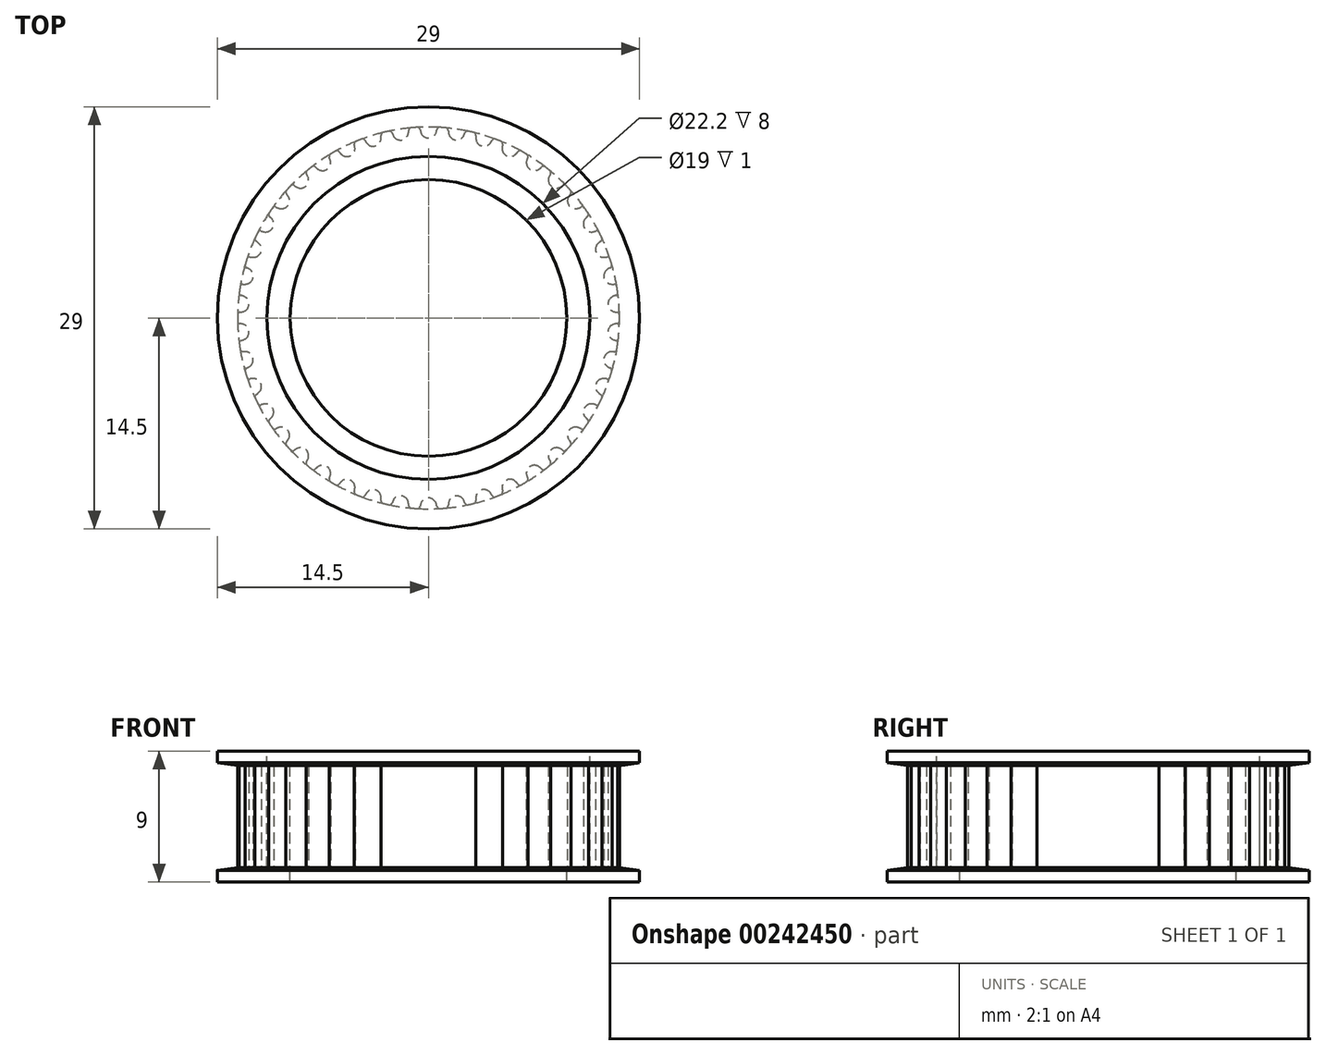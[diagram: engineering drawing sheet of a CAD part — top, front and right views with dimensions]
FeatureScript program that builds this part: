
annotation { "Feature Type Name" : "Feature", "Feature Type Description" : "" }
export const myFeature = defineFeature(function(context is Context, id is Id, definition is map)
    precondition{}
    {
        {
            assignVariable(context, id + "F0", {"name" : "teeth", "anyValue" : 42});
        }
        {
            assignVariable(context, id + "F1", {"name" : "belt_width", "anyValue" : 7});
        }
        {
            var Q0;
            Q0=qCreatedBy(makeId("Top.planeOp"),FACE);
            var sketch = newSketch(context, id + "F2", { "sketchPlane" : qUnion([Q0])});
            skLineSegment(sketch, "E0", {"start": v(0, 0) * mm, "end": v(0, 12.37) * mm, "construction": true});
            skCircle(sketch, "E1", {"center": v(0, 0) * mm, "radius": 13.12 * mm});
            skPoint(sketch, "E2.MirrorCS.end.orphan", {"position": v(0.98, 13.08) * mm});
            skLineSegment(sketch, "E3", {"start": v(0.98, 13.08) * mm, "end": v(1, 13.33) * mm, "construction": true});
            skLineSegment(sketch, "E4", {"start": v(-0.98, 13.08) * mm, "end": v(-1, 13.33) * mm, "construction": true});
            skArc(sketch, "E5", {"start": v(0, 12.37) * mm, "mid": v(0.34, 12.48) * mm, "end": v(0.54, 12.77) * mm});
            skArc(sketch, "E6", {"start": v(0.54, 12.77) * mm, "mid": v(0.56, 12.87) * mm, "end": v(0.58, 12.97) * mm, "construction": true});
            skLineSegment(sketch, "E7", {"start": v(0, 12.37) * mm, "end": v(0, 13.12) * mm, "construction": true});
            skLineSegment(sketch, "E8", {"start": v(0, 13.12) * mm, "end": v(0, 13.37) * mm, "construction": true});
            skArc(sketch, "E9", {"start": v(0.58, 12.97) * mm, "mid": v(0.64, 13.06) * mm, "end": v(0.74, 13.1) * mm, "construction": true});
            skArc(sketch, "E10", {"start": v(1, 13.33) * mm, "mid": v(0, 13.37) * mm, "end": v(-1, 13.33) * mm, "construction": true});
            skLineSegment(sketch, "E11", {"start": v(0.98, 13.08) * mm, "end": v(0.92, 12.33) * mm});
            skLineSegment(sketch, "E12", {"start": v(0.92, 12.33) * mm, "end": v(0, 0) * mm});
            skLineSegment(sketch, "E13", {"start": v(0, 0) * mm, "end": v(-0.92, 12.33) * mm});
            skLineSegment(sketch, "E14", {"start": v(-0.92, 12.33) * mm, "end": v(-0.98, 13.08) * mm});
            skArc(sketch, "E15", {"start": v(0.77, 13.1) * mm, "mid": v(0.65, 13.06) * mm, "end": v(0.58, 12.95) * mm});
            skArc(sketch, "E16", {"start": v(0.54, 12.77) * mm, "mid": v(0.56, 12.86) * mm, "end": v(0.58, 12.95) * mm});
            skArc(sketch, "E17.MirrorCS", {"start": v(0, 12.37) * mm, "mid": v(-0.34, 12.48) * mm, "end": v(-0.54, 12.77) * mm});
            skArc(sketch, "E18.MirrorCS", {"start": v(-0.54, 12.77) * mm, "mid": v(-0.56, 12.86) * mm, "end": v(-0.58, 12.95) * mm});
            skArc(sketch, "E19.MirrorCS", {"start": v(-0.77, 13.1) * mm, "mid": v(-0.65, 13.06) * mm, "end": v(-0.58, 12.95) * mm});
            skArc(sketch, "E20", {"start": v(0, 13.12) * mm, "mid": v(-0.2, 13.11) * mm, "end": v(-0.4, 13.1) * mm});
            skArc(sketch, "E21", {"start": v(0.92, 12.33) * mm, "mid": v(0, 12.37) * mm, "end": v(-0.92, 12.33) * mm, "construction": true});
            skLineSegment(sketch, "E22", {"start": v(1, 13.33) * mm, "end": v(1.03, 13.7) * mm, "construction": true});
            skLineSegment(sketch, "E23", {"start": v(-1, 13.33) * mm, "end": v(-1.03, 13.7) * mm, "construction": true});
            skArc(sketch, "E24", {"start": v(-1.03, 13.7) * mm, "mid": v(0, 13.75) * mm, "end": v(1.03, 13.7) * mm, "construction": true});
            skSolve(sketch);
        }
        {
            var Q0;
            Q0=makeQuery(id+"F2.imprint","IMPRINT",FACE,{"disambiguationData":[TD([[makeQuery(id+"F2.imprint","IMPRINT",EDGE,{"derivedFrom":sQuery(id+"F2.wireOp",EDGE,"E5")}),-1.0]])]});
            var Q1;
            {var subQ1=sQuery(id+"F2.wireOp",EDGE,"E14");Q1=makeQuery(id+"F2.imprint","IMPRINT",FACE,{"disambiguationData":[TD([[makeQuery(id+"F2.imprint","IMPRINT",EDGE,{"derivedFrom":subQ1}),-1.0]])]});}
            var Q2;
            {var subQ0=sQuery(id+"F2.wireOp",EDGE,"E12");Q2=makeQuery(id+"F2.imprint","IMPRINT",FACE,{"disambiguationData":[TD([[makeQuery(id+"F2.imprint","IMPRINT",EDGE,{"derivedFrom":subQ0}),-1.0]])]});}
            extrude(context, id + "F3", {"entities" : qUnion([Q0, Q1, Q2]), "depth" : (getVariable(context, 'belt_width')) * mm, "symmetric" : true});
        }
        {
            var Q0;
            Q0=makeQuery(id+"F3.opExtrude","SWEPT_BODY",BODY,{"disambiguationData":[OSD([sQuery(id+"F2.wireOp",EDGE,"E1"),sQuery(id+"F2.wireOp",EDGE,"E5"),sQuery(id+"F2.wireOp",EDGE,"E11"),sQuery(id+"F2.wireOp",EDGE,"E12"),sQuery(id+"F2.wireOp",EDGE,"E13"),sQuery(id+"F2.wireOp",EDGE,"E14"),sQuery(id+"F2.wireOp",EDGE,"E15"),sQuery(id+"F2.wireOp",EDGE,"E16"),sQuery(id+"F2.wireOp",EDGE,"E17.MirrorCS"),sQuery(id+"F2.wireOp",EDGE,"E18.MirrorCS"),sQuery(id+"F2.wireOp",EDGE,"E19.MirrorCS")])]});
            var Q1;
            Q1=makeQuery(id+"F3.opExtrude","SWEPT_EDGE",EDGE,{"disambiguationData":[OSD([sQuery(id+"F2.wireOp",EDGE,"E12"),sQuery(id+"F2.wireOp",EDGE,"E13")])]});
            circularPattern(context, id + "F4", {"operationType" : NewBodyOperationType.ADD, "entities" : qUnion([Q0]), "axis" : qUnion([Q1]), "angle" : 360 * degree, "instanceCount" : getVariable(context, 'teeth'), "equalSpace" : true, "computeTransformsWithoutBuiltin" : true});
        }
        {
            var Q0;
            Q0=qCreatedBy(makeId("Front.planeOp"),FACE);
            var sketch = newSketch(context, id + "F5", { "sketchPlane" : qUnion([Q0])});
            skLineSegment(sketch, "E25", {"start": v(0, -3.5) * mm, "end": v(13.12, -3.5) * mm});
            skLineSegment(sketch, "E26", {"start": v(13.12, -3.5) * mm, "end": v(14.5, -3.7) * mm});
            skLineSegment(sketch, "E27", {"start": v(0, 3.5) * mm, "end": v(13.12, 3.5) * mm});
            skLineSegment(sketch, "E28", {"start": v(14.5, 3.7) * mm, "end": v(13.12, 3.5) * mm});
            skLineSegment(sketch, "E29", {"start": v(14.5, 3.7) * mm, "end": v(14.5, 4.5) * mm});
            skLineSegment(sketch, "E30", {"start": v(14.5, 4.5) * mm, "end": v(0, 4.5) * mm});
            skLineSegment(sketch, "E31", {"start": v(0, 4.5) * mm, "end": v(0, 3.5) * mm});
            skLineSegment(sketch, "E32", {"start": v(13.12, -3.5) * mm, "end": v(14.5, -3.5) * mm, "construction": true});
            skLineSegment(sketch, "E33", {"start": v(14.5, -3.5) * mm, "end": v(14.5, -3.7) * mm, "construction": true});
            skLineSegment(sketch, "E34", {"start": v(13.12, 3.5) * mm, "end": v(14.5, 3.5) * mm, "construction": true});
            skLineSegment(sketch, "E35", {"start": v(14.5, 3.5) * mm, "end": v(14.5, 3.7) * mm, "construction": true});
            skLineSegment(sketch, "E36", {"start": v(13.12, 0) * mm, "end": v(13.12, -3.5) * mm, "construction": true});
            skLineSegment(sketch, "E37", {"start": v(14.5, -4.5) * mm, "end": v(0, -4.5) * mm});
            skLineSegment(sketch, "E38", {"start": v(14.5, -3.7) * mm, "end": v(14.5, -4.5) * mm});
            skLineSegment(sketch, "E39", {"start": v(0, -3.5) * mm, "end": v(0, -4.5) * mm});
            skLineSegment(sketch, "E40", {"start": v(0, 4.5) * mm, "end": v(0, -4.5) * mm, "construction": true});
            skSolve(sketch);
        }
        {
            var Q0;
            Q0=makeQuery(id+"F5.imprint","IMPRINT",FACE,{"disambiguationData":[TD([[makeQuery(id+"F5.imprint","IMPRINT",EDGE,{"derivedFrom":sQuery(id+"F5.wireOp",EDGE,"E25")}),-1.0]])]});
            var Q1;
            Q1=makeQuery(id+"F5.imprint","IMPRINT",FACE,{"disambiguationData":[TD([[makeQuery(id+"F5.imprint","IMPRINT",EDGE,{"derivedFrom":sQuery(id+"F5.wireOp",EDGE,"E27")}),1.0]])]});
            var Q2;
            Q2=qConstructionFilter(qBodyType(qCreatedBy(id+"F5",EDGE),BodyType.WIRE),ConstructionObject.NO);
            var Q3;
            Q3=sQuery(id+"F5.wireOp",EDGE,"E40");
            revolve(context, id + "F6", {"operationType" : NewBodyOperationType.ADD, "entities" : qUnion([Q0, Q1]), "surfaceEntities" : qUnion([Q2]), "axis" : qUnion([Q3]), "revolveType" : RevolveType.FULL});
        }
        {
            var Q0;
            Q0=makeQuery(id+"F6.opRevolve","SWEPT_FACE",FACE,{"disambiguationData":[OSD([sQuery(id+"F5.wireOp",EDGE,"E30")])]});
            var sketch = newSketch(context, id + "F7", { "sketchPlane" : qUnion([Q0])});
            skPoint(sketch, "E41", {"position": v(0, 0) * mm});
            skCircle(sketch, "E42", {"center": v(0, 0) * mm, "radius": 11.1 * mm});
            skCircle(sketch, "E43", {"center": v(0, 0) * mm, "radius": 9.5 * mm});
            skSolve(sketch);
        }
        {
            var Q0;
            Q0=makeQuery(id+"F7.imprint","IMPRINT",FACE,{"disambiguationData":[TD([[makeQuery(id+"F7.imprint","IMPRINT",EDGE,{"derivedFrom":sQuery(id+"F7.wireOp",EDGE,"E42")}),1.0]])]});
            extrude(context, id + "F8", {"entities" : qUnion([Q0]), "operationType" : NewBodyOperationType.REMOVE, "oppositeDirection" : true, "depth" : 8 * mm});
        }
        {
            var Q0;
            Q0=makeQuery(id+"F8.boolean.opBoolean","SPLIT",FACE,{"disambiguationData":[TD([makeQuery(id+"F8.opExtrude","SWEPT_FACE",FACE,{"disambiguationData":[OSD([sQuery(id+"F7.wireOp",EDGE,"E43")])]})])],"derivedFrom":makeQuery(id+"F6.opRevolve","SWEPT_FACE",FACE,{"disambiguationData":[OSD([sQuery(id+"F5.wireOp",EDGE,"E30")])]})});
            extrude(context, id + "F9", {"entities" : qUnion([Q0]), "operationType" : NewBodyOperationType.REMOVE, "endBound" : BoundingType.UP_TO_NEXT, "oppositeDirection" : true, "depth" : 25 * mm});
        }
    });
